# Revit family: Layout-Teknion-Zones_Workshop_Tables_03-R2022
name_source: partatom
category: Furniture Systems
units: mm (PartAtom-declared; Revit-internal decimal feet)

## family parameters
Always vertical = Yes
Cut with Voids When Loaded = No
OmniClass Number = 23.40.70.14.64.21
OmniClass Title = Systems Furniture
Part Type = Normal
Room Calculation Point = No
Round Connector Dimension = Use Diameter
Shared = No
Work Plane-Based = No

## types (1)
- Workshop Tables
    Apparent Load = 42 VA
    Apparent Load Note = With 1 Table Lamp = 21VA, With 2 Table Lamps = 42VA - Without Table Lamps = 0 VA
    Assembly Code = E2020200
    Connector Description = Power Connector
    Default Elevation = 0' - 0"
    Depth = 8' - 9 1/2"
    Description = 12'  9 1/2" x 8'  9 1/2"
    Height = 3' - 5 15/32"
    Manufacturer = Teknion
    Manufacturer Fax = 416.661.4586
    Model = Workshop Tables 03
    Product Line = Zones
    Product Page URL = http://teknionplanningtool.com
    Series = Zones
    Sustainability Data = http://www.teknion.com
    URL = http://www.teknion.com
    Voltage = 120 V
    Voltage Note = With Table Lamps = 120 V - Without Table Lamps = 0 V
    Warranty = http://www.teknion.com
    Width = 12' - 9 15/32"

## geometry (parser evidence)
native form markers: Blend x56, Sweep x25
no freeform markers — native parametric forms only
